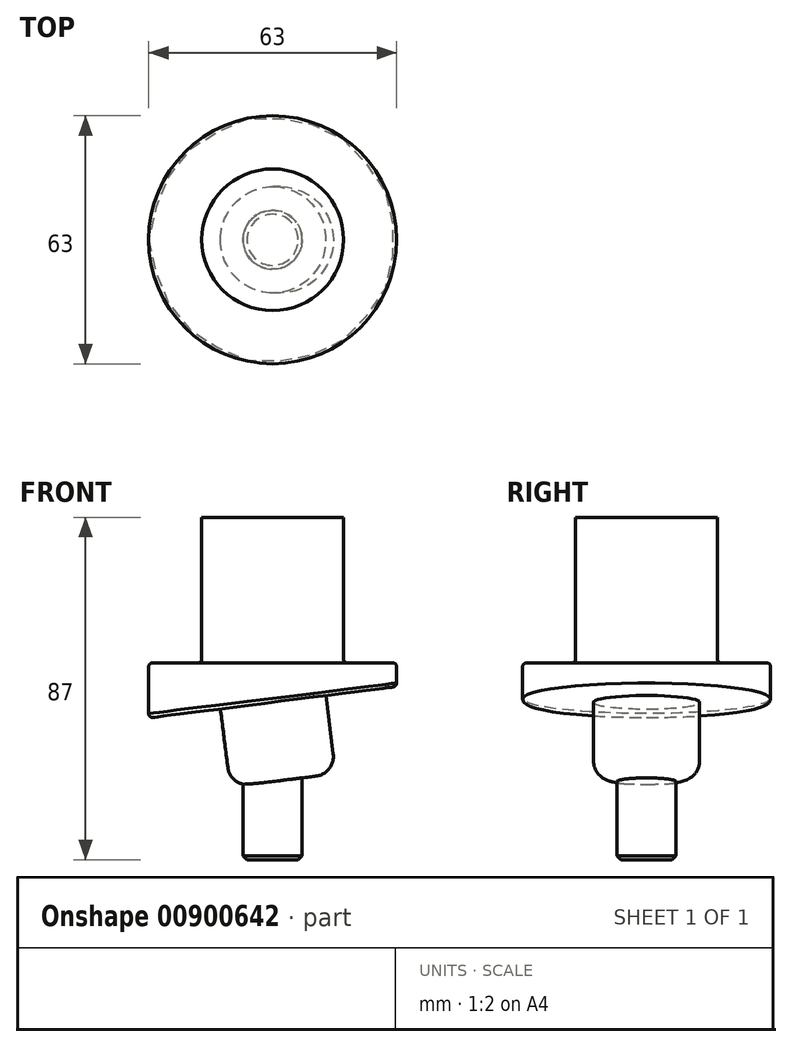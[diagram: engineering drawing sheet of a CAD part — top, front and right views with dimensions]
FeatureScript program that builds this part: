
annotation { "Feature Type Name" : "Feature", "Feature Type Description" : "" }
export const myFeature = defineFeature(function(context is Context, id is Id, definition is map)
    precondition{}
    {
        {
            var Q0;
            Q0=qCreatedBy(makeId("Front.planeOp"),FACE);
            var sketch = newSketch(context, id + "F0", { "sketchPlane" : qUnion([Q0])});
            skLineSegment(sketch, "E0", {"start": v(0, 0) * mm, "end": v(0, 49) * mm, "construction": true});
            skLineSegment(sketch, "E1.bottom", {"start": v(0, 0) * mm, "end": v(31.5, 0) * mm});
            skLineSegment(sketch, "E1.right", {"start": v(31.5, 0) * mm, "end": v(31.5, 14) * mm});
            skLineSegment(sketch, "E2.top", {"start": v(0, 51) * mm, "end": v(18, 51) * mm});
            skLineSegment(sketch, "E2.right", {"start": v(18, 14) * mm, "end": v(18, 51) * mm});
            skLineSegment(sketch, "E3.trimOffspring", {"start": v(18, 14) * mm, "end": v(31.5, 14) * mm});
            skLineSegment(sketch, "E4", {"start": v(0, 51) * mm, "end": v(0, 0) * mm});
            skPoint(sketch, "E5.orphan", {"position": v(-18, 51) * mm});
            skPoint(sketch, "E6.orphan", {"position": v(-31.5, 0) * mm});
            skSolve(sketch);
        }
        {
            var Q0;
            Q0=makeQuery(id+"F0.imprint","IMPRINT",FACE,{"disambiguationData":[TD([[makeQuery(id+"F0.imprint","IMPRINT",EDGE,{"derivedFrom":sQuery(id+"F0.wireOp",EDGE,"E1.bottom")}),1.0]])]});
            var Q1;
            Q1=sQuery(id+"F0.wireOp",EDGE,"E0");
            revolve(context, id + "F1", {"surfaceOperationType" : NewSurfaceOperationType.NEW, "entities" : qUnion([Q0]), "axis" : qUnion([Q1]), "revolveType" : RevolveType.FULL});
        }
        {
            var Q0;
            Q0=qCreatedBy(makeId("Front.planeOp"),FACE);
            var sketch = newSketch(context, id + "F2", { "sketchPlane" : qUnion([Q0])});
            skLineSegment(sketch, "E7", {"start": v(-31.5, 0) * mm, "end": v(31.5, 8) * mm});
            skLineSegment(sketch, "E8", {"start": v(31.5, 8) * mm, "end": v(31.5, 0) * mm});
            skLineSegment(sketch, "E9", {"start": v(31.5, 0) * mm, "end": v(-31.5, 0) * mm});
            skLineSegment(sketch, "E10", {"start": v(39.92, 8) * mm, "end": v(14.72, 8) * mm, "construction": true});
            skSolve(sketch);
        }
        {
            var Q0;
            Q0 = qSketchRegion(id + "F2", true);
            extrude(context, id + "F3", {"entities" : qUnion([Q0]), "operationType" : NewBodyOperationType.REMOVE, "oppositeDirection" : true, "depth" : 100 * mm, "offsetDistance" : 25 * mm, "symmetric" : true});
        }
        {
            var Q0;
            Q0=makeQuery(id+"F3.boolean.opBoolean","INTERSECT",EDGE,{"derivedFrom":[makeQuery(id+"F1.opRevolve","SWEPT_FACE",FACE,{"disambiguationData":[OSD([sQuery(id+"F0.wireOp",EDGE,"E1.right")])]}),makeQuery(id+"F3.opExtrude","SWEPT_FACE",FACE,{"disambiguationData":[OSD([sQuery(id+"F2.wireOp",EDGE,"E7")])]})]});
            var Q1;
            Q1=makeQuery(id+"F1.opRevolve","SWEPT_EDGE",EDGE,{"disambiguationData":[OSD([sQuery(id+"F0.wireOp",EDGE,"E1.right"),sQuery(id+"F0.wireOp",EDGE,"E3.trimOffspring")])]});
            var Q2;
            Q2=makeQuery(id+"F1.opRevolve","SWEPT_EDGE",EDGE,{"disambiguationData":[OSD([sQuery(id+"F0.wireOp",EDGE,"E2.right"),sQuery(id+"F0.wireOp",EDGE,"E3.trimOffspring")])]});
            fillet(context, id + "F4", {"entities" : qUnion([Q0, Q1, Q2]), "radius" : 1 * mm, "tangentPropagation" : true, "allowEdgeOverflow" : false});
        }
        {
            var Q0;
            Q0=makeQuery(id+"F3.boolean.opBoolean","COPY",FACE,{"derivedFrom":makeQuery(id+"F3.opExtrude","SWEPT_FACE",FACE,{"disambiguationData":[OSD([sQuery(id+"F2.wireOp",EDGE,"E7")])]})});
            var sketch = newSketch(context, id + "F5", { "sketchPlane" : qUnion([Q0])});
            skCircle(sketch, "E11", {"center": v(0.63, 0) * mm, "radius": 13.5 * mm});
            skSolve(sketch);
        }
        {
            var Q0;
            Q0=makeQuery(id+"F5.imprint","IMPRINT",FACE,{"disambiguationData":[TD([[makeQuery(id+"F5.imprint","IMPRINT",EDGE,{"derivedFrom":sQuery(id+"F5.wireOp",EDGE,"E11")}),1.0]])]});
            extrude(context, id + "F6", {"entities" : qUnion([Q0]), "operationType" : NewBodyOperationType.ADD, "depth" : 20 * mm, "offsetDistance" : 25 * mm});
        }
        {
            var Q0;
            Q0=makeQuery(id+"F6.opExtrude","CAP_EDGE",EDGE,{"disambiguationData":[OSD([sQuery(id+"F5.wireOp",EDGE,"E11")])],"isStart":false});
            fillet(context, id + "F7", {"entities" : qUnion([Q0]), "radius" : 5 * mm, "tangentPropagation" : true, "allowEdgeOverflow" : false});
        }
        {
            var Q0;
            Q0=makeQuery(id+"F1.opRevolve","SWEPT_FACE",FACE,{"disambiguationData":[OSD([sQuery(id+"F0.wireOp",EDGE,"E2.top")])]});
            var sketch = newSketch(context, id + "F8", { "sketchPlane" : qUnion([Q0])});
            skCircle(sketch, "E12", {"center": v(0, 0) * mm, "radius": 7.5 * mm});
            skSolve(sketch);
        }
        {
            var Q0;
            Q0=makeQuery(id+"F8.imprint","IMPRINT",FACE,{"disambiguationData":[TD([[makeQuery(id+"F8.imprint","IMPRINT",EDGE,{"derivedFrom":sQuery(id+"F8.wireOp",EDGE,"E12")}),1.0]])]});
            extrude(context, id + "F9", {"entities" : qUnion([Q0]), "operationType" : NewBodyOperationType.ADD, "oppositeDirection" : true, "depth" : 87 * mm, "offsetDistance" : 25 * mm});
        }
        {
            var Q0;
            Q0=makeQuery(id+"F9.opExtrude","CAP_EDGE",EDGE,{"disambiguationData":[OSD([sQuery(id+"F8.wireOp",EDGE,"E12")])],"isStart":false});
            chamfer(context, id + "F10", {"entities" : qUnion([Q0]), "width" : 1 * mm, "tangentPropagation" : true});
        }
    });
